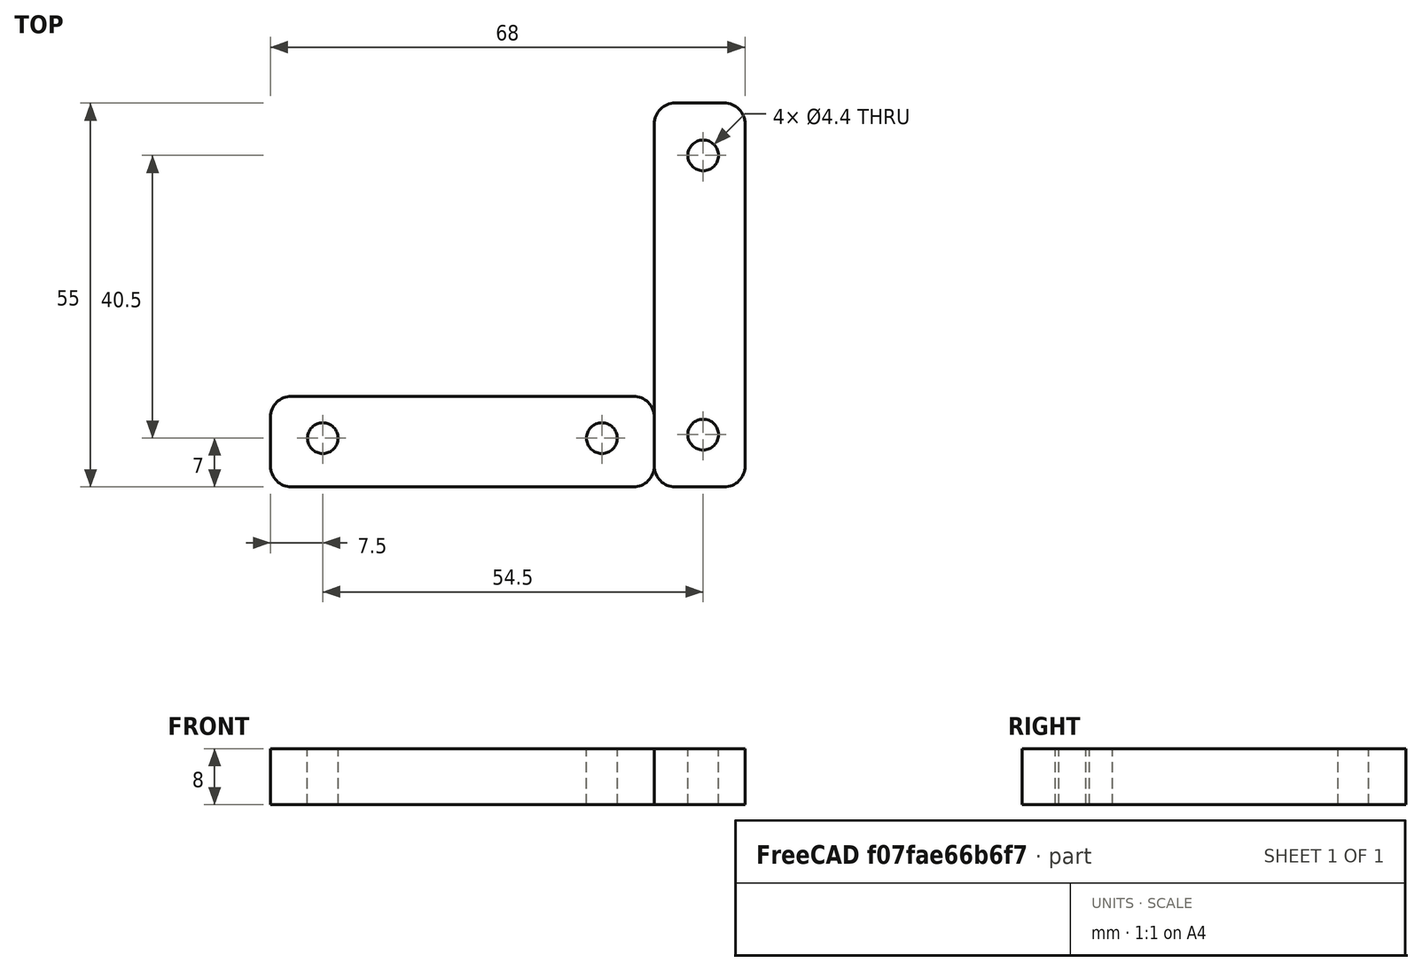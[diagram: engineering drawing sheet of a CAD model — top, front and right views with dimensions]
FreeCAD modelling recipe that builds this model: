
FCSTD DOCUMENT  (FreeCAD 0.15R4527 (Git))
Label: x_holder_reinforcement
License: All rights reserved
LicenseURL: http://en.wikipedia.org/wiki/All_rights_reserved
objects: Part::Feature×2, Part::Cylinder×2, Mesh::Feature×1, Part::Box×1, Part::MultiFuse×1, Part::Cut×1, Part::Fillet×1
note: 8 computed .brp shape members not serialized (recipe doc carries the construction recipe); baked Part::Feature solids carry a one-line shape summary decoded from their .brp

FEATURE [Mesh::Feature] reinforcement
FEATURE [Part::Feature] reinforcement001001  label="reinforcement002"
  shape: bbox 13 x 55 x 8.016 mm, 258 faces, 0 solids (baked)
FEATURE [Part::Box] Box  label="Cubo"
  Height = 8
  Length = 13
  Width = 55
FEATURE [Part::Cylinder] Cylinder  label="Cilindro"
  Angle = 360
  Height = 10
  Placement = pos=(7,7.5,0) rot=(0,0,1;0rad)
  Radius = 2.2
FEATURE [Part::Cylinder] Cylinder001  label="Cilindro001"
  Angle = 360
  Height = 10
  Placement = pos=(7,47.5,0) rot=(0,0,1;0rad)
  Radius = 2.2
FEATURE [Part::MultiFuse] Fusion  label="screw_holes"
  Shapes = -> [Cylinder,Cylinder001]
FEATURE [Part::Cut] Cut
  Base = -> Box
  Tool = -> Fusion
FEATURE [Part::Fillet] Fillet  label="x_holder_reinforcement"
  Base = -> Cut
  Edges = 4 edges r=3: [Edge1,Edge3,Edge6,Edge13]
FEATURE [Part::Feature] Fillet001  label="x_holder_reinforcement001"
  Placement = pos=(0,0,0) rot=(0,0,1;1.5708rad)
  shape: bbox 55 x 13 x 8 mm, 12 faces (baked)
